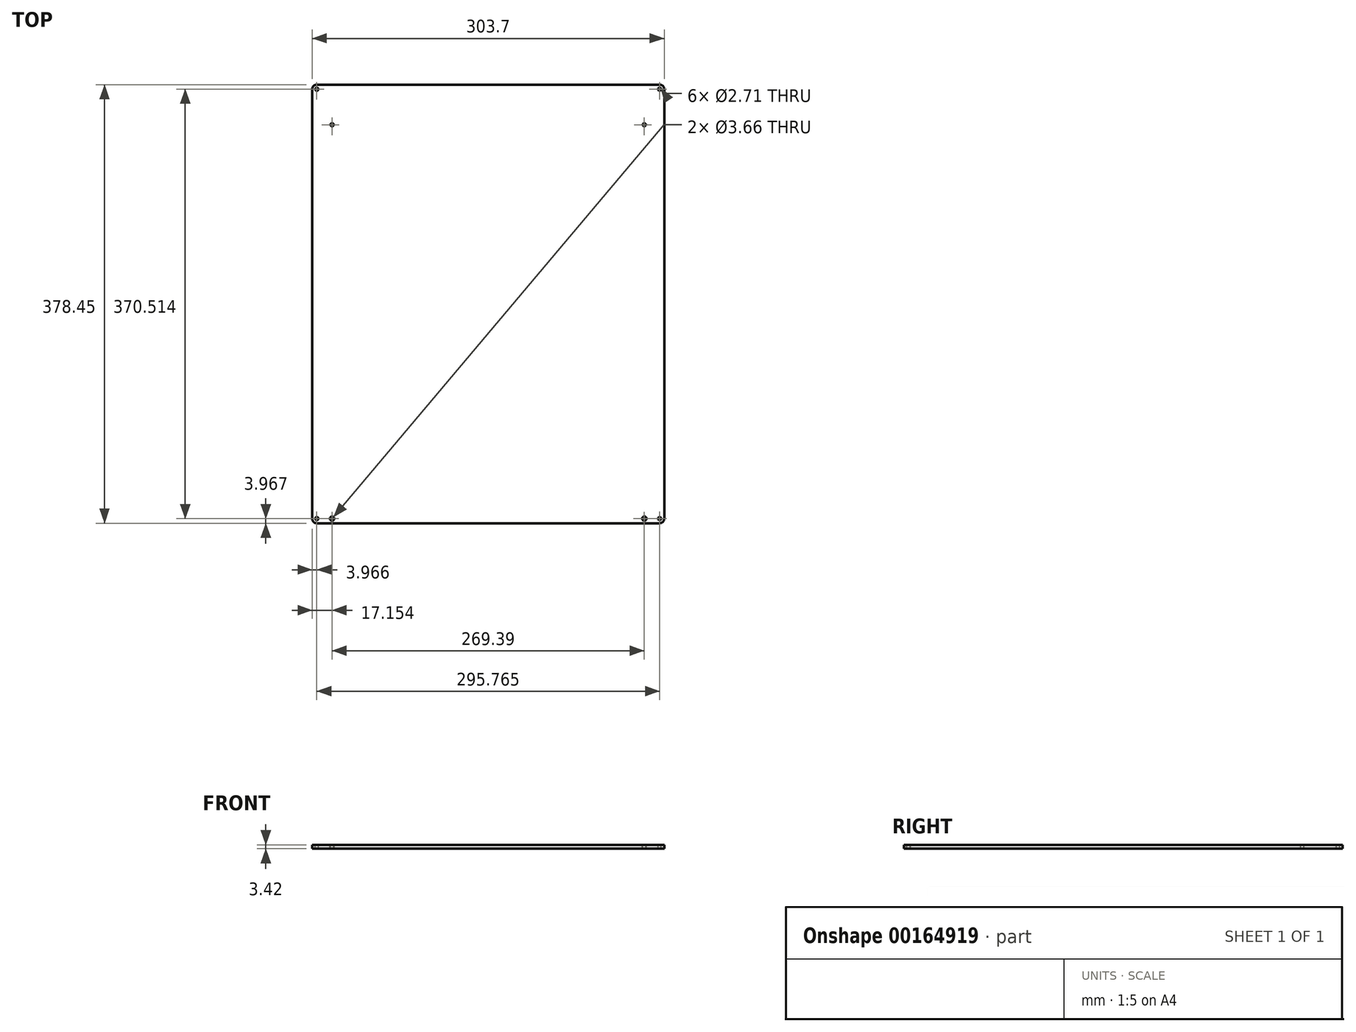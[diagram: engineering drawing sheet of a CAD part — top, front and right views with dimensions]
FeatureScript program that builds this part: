
annotation { "Feature Type Name" : "Feature", "Feature Type Description" : "" }
export const myFeature = defineFeature(function(context is Context, id is Id, definition is map)
    precondition{}
    {
        {
            var Q0;
            Q0=qCreatedBy(makeId("Top.planeOp"),FACE);
            var sketch = newSketch(context, id + "F0", { "sketchPlane" : qUnion([Q0])});
            skLineSegment(sketch, "E0.bottom", {"start": v(0, 0) * mm, "end": v(-303.7, 0) * mm});
            skLineSegment(sketch, "E0.top", {"start": v(0, -378.45) * mm, "end": v(-303.7, -378.45) * mm});
            skLineSegment(sketch, "E0.left", {"start": v(0, 0) * mm, "end": v(0, -378.45) * mm});
            skLineSegment(sketch, "E0.right", {"start": v(-303.7, 0) * mm, "end": v(-303.7, -378.45) * mm});
            skSolve(sketch);
        }
        {
            var Q0;
            Q0=qSketchRegion(id+"F0",true);
            extrude(context, id + "F1", {"entities" : qUnion([Q0]), "depth" : 3.42 * mm});
        }
        {
            var Q0;
            Q0=makeQuery(id+"F1.opExtrude","SWEPT_EDGE",EDGE,{"disambiguationData":[OSD([sQuery(id+"F0.wireOp",EDGE,"E0.bottom"),sQuery(id+"F0.wireOp",EDGE,"E0.right")])]});
            var Q1;
            Q1=makeQuery(id+"F1.opExtrude","SWEPT_EDGE",EDGE,{"disambiguationData":[OSD([sQuery(id+"F0.wireOp",EDGE,"E0.top"),sQuery(id+"F0.wireOp",EDGE,"E0.right")])]});
            var Q2;
            Q2=makeQuery(id+"F1.opExtrude","SWEPT_EDGE",EDGE,{"disambiguationData":[OSD([sQuery(id+"F0.wireOp",EDGE,"E0.top"),sQuery(id+"F0.wireOp",EDGE,"E0.left")])]});
            var Q3;
            Q3=makeQuery(id+"F1.opExtrude","SWEPT_EDGE",EDGE,{"disambiguationData":[OSD([sQuery(id+"F0.wireOp",EDGE,"E0.bottom"),sQuery(id+"F0.wireOp",EDGE,"E0.left")])]});
            fillet(context, id + "F2", {"entities" : qUnion([Q0, Q1, Q2, Q3]), "radius" : 3.97 * mm, "tangentPropagation" : true, "allowEdgeOverflow" : false});
        }
        {
            var Q0;
            Q0=makeQuery(id+"F1.opExtrude","CAP_FACE",FACE,{"disambiguationData":[OSD([sQuery(id+"F0.wireOp",EDGE,"E0.bottom"),sQuery(id+"F0.wireOp",EDGE,"E0.top"),sQuery(id+"F0.wireOp",EDGE,"E0.left"),sQuery(id+"F0.wireOp",EDGE,"E0.right")])],"isStart":false});
            var sketch = newSketch(context, id + "F3", { "sketchPlane" : qUnion([Q0])});
            skCircle(sketch, "E1", {"center": v(-299.73, -3.97) * mm, "radius": 1.35 * mm});
            skCircle(sketch, "E2", {"center": v(-3.97, -3.97) * mm, "radius": 1.35 * mm});
            skCircle(sketch, "E3", {"center": v(-299.73, -374.48) * mm, "radius": 1.35 * mm});
            skCircle(sketch, "E4", {"center": v(-3.97, -374.48) * mm, "radius": 1.35 * mm});
            skLineSegment(sketch, "E5", {"start": v(-286.55, -34.63) * mm, "end": v(-17.16, -34.63) * mm, "construction": true});
            skCircle(sketch, "E6", {"center": v(-286.55, -34.63) * mm, "radius": 1.35 * mm});
            skCircle(sketch, "E7", {"center": v(-17.16, -34.63) * mm, "radius": 1.35 * mm});
            skLineSegment(sketch, "E8", {"start": v(-151.85, 0) * mm, "end": v(-151.85, -34.63) * mm, "construction": true});
            skSolve(sketch);
        }
        {
            var Q0;
            Q0=qSketchRegion(id+"F3",true);
            var Q1;
            Q1=makeQuery(id+"F1.opExtrude","CAP_FACE",FACE,{"disambiguationData":[OSD([sQuery(id+"F0.wireOp",EDGE,"E0.bottom"),sQuery(id+"F0.wireOp",EDGE,"E0.top"),sQuery(id+"F0.wireOp",EDGE,"E0.left"),sQuery(id+"F0.wireOp",EDGE,"E0.right")])],"isStart":true});
            extrude(context, id + "F4", {"entities" : qUnion([Q0]), "operationType" : NewBodyOperationType.REMOVE, "endBound" : BoundingType.UP_TO_SURFACE, "oppositeDirection" : true, "endBoundEntityFace" : qUnion([Q1]), "depth" : 25.4 * mm});
        }
        {
            var Q0;
            Q0=makeQuery(id+"F1.opExtrude","CAP_FACE",FACE,{"disambiguationData":[OSD([sQuery(id+"F0.wireOp",EDGE,"E0.bottom"),sQuery(id+"F0.wireOp",EDGE,"E0.top"),sQuery(id+"F0.wireOp",EDGE,"E0.left"),sQuery(id+"F0.wireOp",EDGE,"E0.right")])],"isStart":false});
            var sketch = newSketch(context, id + "F5", { "sketchPlane" : qUnion([Q0])});
            skLineSegment(sketch, "E9", {"start": v(-299.73, -374.48) * mm, "end": v(-286.55, -374.48) * mm, "construction": true});
            skLineSegment(sketch, "E10.bottom", {"start": v(-286.55, -374.48) * mm, "end": v(-17.16, -374.48) * mm, "construction": true});
            skCircle(sketch, "E11", {"center": v(-286.55, -374.48) * mm, "radius": 1.83 * mm});
            skCircle(sketch, "E12", {"center": v(-17.16, -374.48) * mm, "radius": 1.83 * mm});
            skLineSegment(sketch, "E13", {"start": v(-17.16, -374.48) * mm, "end": v(-3.97, -374.48) * mm, "construction": true});
            skSolve(sketch);
        }
        {
            var Q0;
            Q0=qSketchRegion(id+"F5",true);
            var Q1;
            Q1=makeQuery(id+"F1.opExtrude","CAP_FACE",FACE,{"disambiguationData":[OSD([sQuery(id+"F0.wireOp",EDGE,"E0.bottom"),sQuery(id+"F0.wireOp",EDGE,"E0.top"),sQuery(id+"F0.wireOp",EDGE,"E0.left"),sQuery(id+"F0.wireOp",EDGE,"E0.right")])],"isStart":true});
            extrude(context, id + "F6", {"entities" : qUnion([Q0]), "operationType" : NewBodyOperationType.REMOVE, "endBound" : BoundingType.UP_TO_SURFACE, "oppositeDirection" : true, "endBoundEntityFace" : qUnion([Q1]), "depth" : 25.4 * mm});
        }
    });
